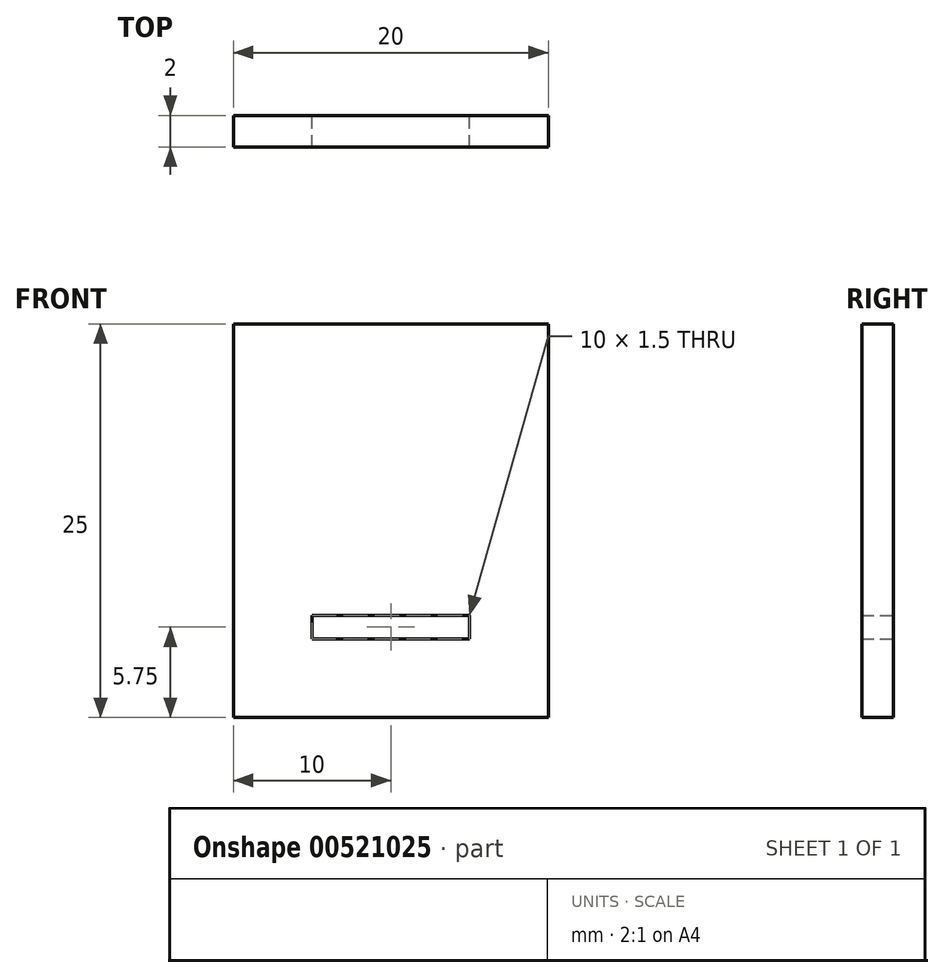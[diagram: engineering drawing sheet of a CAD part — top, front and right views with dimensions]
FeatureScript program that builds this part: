
annotation { "Feature Type Name" : "Feature", "Feature Type Description" : "" }
export const myFeature = defineFeature(function(context is Context, id is Id, definition is map)
    precondition{}
    {
        {
            var Q0;
            Q0=qCreatedBy(makeId("Front.planeOp"),FACE);
            var sketch = newSketch(context, id + "F0", { "sketchPlane" : qUnion([Q0])});
            skLineSegment(sketch, "E0.bottom", {"start": v(-10, 10) * mm, "end": v(10, 10) * mm});
            skLineSegment(sketch, "E0.top", {"start": v(-5, -10) * mm, "end": v(5, -10) * mm});
            skLineSegment(sketch, "E0.left", {"start": v(-10, 10) * mm, "end": v(-10, -10) * mm});
            skLineSegment(sketch, "E0.right", {"start": v(10, 10) * mm, "end": v(10, -10) * mm});
            skPoint(sketch, "E0.middle", {"position": v(0, 0) * mm});
            skLineSegment(sketch, "E1.bottom", {"start": v(0, -10) * mm, "end": v(-5, -10) * mm});
            skLineSegment(sketch, "E1.top", {"start": v(0, -8.5) * mm, "end": v(-5, -8.5) * mm});
            skLineSegment(sketch, "E1.right", {"start": v(-5, -10) * mm, "end": v(-5, -8.5) * mm});
            skLineSegment(sketch, "E2.MirrorCS", {"start": v(0, -8.5) * mm, "end": v(5, -8.5) * mm});
            skLineSegment(sketch, "E3.MirrorCS", {"start": v(5, -10) * mm, "end": v(5, -8.5) * mm});
            skPoint(sketch, "E4.MirrorCS.end.orphan", {"position": v(-5, -8.5) * mm});
            skPoint(sketch, "E4.MirrorCS.start.orphan", {"position": v(-10, -8.5) * mm});
            skLineSegment(sketch, "E5", {"start": v(10, -10) * mm, "end": v(10, -15) * mm});
            skLineSegment(sketch, "E6", {"start": v(-10, -10) * mm, "end": v(-10, -15) * mm});
            skLineSegment(sketch, "E7", {"start": v(-10, -15) * mm, "end": v(10, -15) * mm});
            skSolve(sketch);
        }
        {
            var Q0;
            Q0=makeQuery(id+"F0.imprint","IMPRINT",FACE,{"disambiguationData":[TD([[makeQuery(id+"F0.imprint","IMPRINT",EDGE,{"derivedFrom":sQuery(id+"F0.wireOp",EDGE,"E0.bottom")}),-1.0]])]});
            extrude(context, id + "F1", {"entities" : qUnion([Q0]), "depth" : 2 * mm, "offsetDistance" : 25 * mm});
        }
    });
